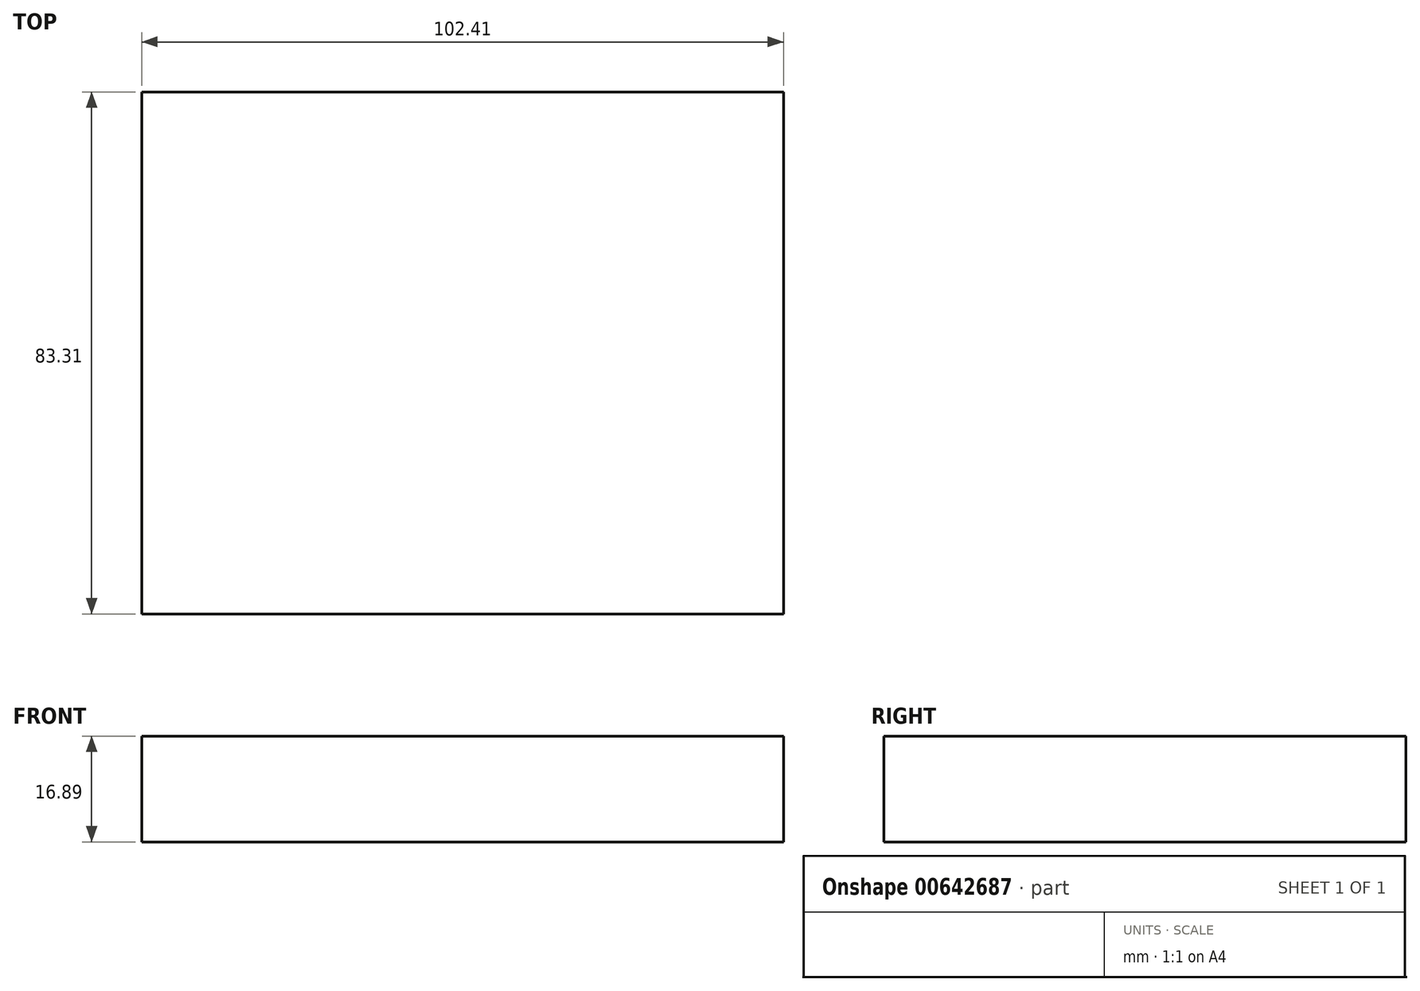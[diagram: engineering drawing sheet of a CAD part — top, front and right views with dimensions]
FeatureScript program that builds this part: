
annotation { "Feature Type Name" : "Feature", "Feature Type Description" : "" }
export const myFeature = defineFeature(function(context is Context, id is Id, definition is map)
    precondition{}
    {
        {
            var Q0;
            Q0=qCreatedBy(makeId("Front.planeOp"),FACE);
            var sketch = newSketch(context, id + "F0", { "sketchPlane" : qUnion([Q0])});
            skLineSegment(sketch, "E0.bottom", {"start": v(-64.26, 25.7) * mm, "end": v(38.15, 25.7) * mm});
            skLineSegment(sketch, "E0.top", {"start": v(-64.26, 8.8) * mm, "end": v(38.15, 8.8) * mm});
            skLineSegment(sketch, "E0.left", {"start": v(-64.26, 25.7) * mm, "end": v(-64.26, 8.8) * mm});
            skLineSegment(sketch, "E0.right", {"start": v(38.15, 25.7) * mm, "end": v(38.15, 8.8) * mm});
            skSolve(sketch);
        }
        {
            var Q0;
            Q0=makeQuery(id+"F0.imprint","IMPRINT",FACE,{"disambiguationData":[TD([[makeQuery(id+"F0.imprint","IMPRINT",EDGE,{"derivedFrom":sQuery(id+"F0.wireOp",EDGE,"E0.bottom")}),-1.0]])]});
            extrude(context, id + "F1", {"entities" : qUnion([Q0]), "depth" : 83.31 * mm, "offsetDistance" : 25.4 * mm});
        }
    });
